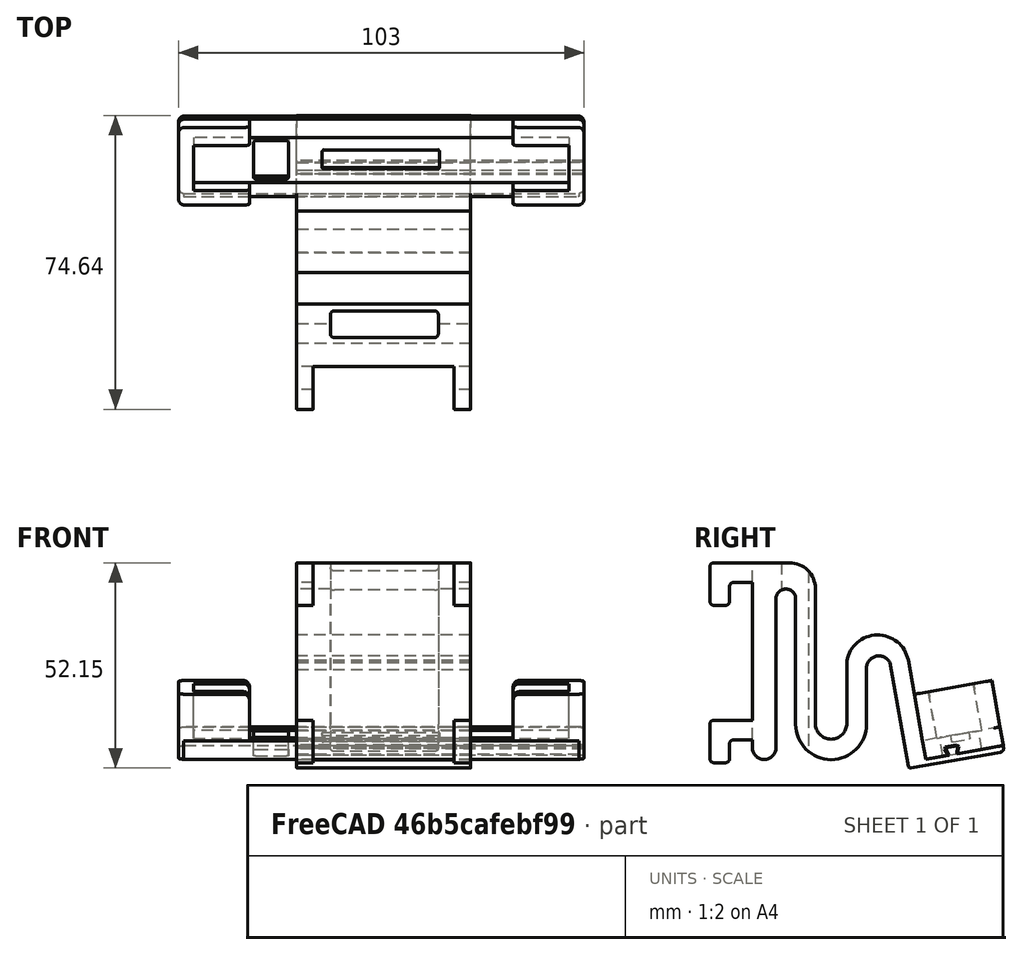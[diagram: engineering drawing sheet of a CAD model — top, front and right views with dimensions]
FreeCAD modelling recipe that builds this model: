
FCSTD DOCUMENT  (FreeCAD 1.1R20260414 (Git shallow))
Label: insight_skadis_holder_2
License: All rights reserved
LicenseURL: https://en.wikipedia.org/wiki/All_rights_reserved
objects: Sketcher::SketchObject×9, PartDesign::Fillet×7, PartDesign::Pocket×5, PartDesign::Pad×4, App::Point×2, PartDesign::Plane×2, PartDesign::Body×2, Part::Feature×1, Spreadsheet::Sheet×1, PartDesign::LinearPattern×1, Mesh::Feature×1
note: 73 computed .brp shape members not serialized (recipe doc carries the construction recipe); baked Part::Feature solids carry a one-line shape summary decoded from their .brp

FEATURE [App::Point] Origin001
  Role = Origin
FEATURE [Part::Feature] Path  label="Svg Import from Figma"
  Placement = pos=(0,0,0) rot=(0.57735,0.57735,0.57735;2.0944rad)
  shape: bbox 2e-07 x 45 x 37.5 mm, 1 faces, 0 solids (baked)
FEATURE [Spreadsheet::Sheet] Spreadsheet
  cells = A1='SkadisOffset; B1(SkadisOffset)=0.8; A2='SkadisHoleWidth; B2(SkadisHoleWidth)=5; A3='SkadisHoleHeight; B3(SkadisHoleHeight)=15; A4='SkadisHoleDistance; B4(SkadisHoleDistance)=35; A5='DeviceWidth; B5(DeviceWidth)=97; A6='DeviceDepth; B6(DeviceDepth)=14; A7='HolderWidth; B7(HolderWidth)==SkadisHoleDistance + HookThikness * 2 + SkadisOffset; A11='HookThikness; B11(HookThikness)==SkadisHoleWidth - SkadisOffset; C11='толщина в фас; A12='HookThiknessSide; B12(HookThiknessSide)==SkadisHoleHeight / 3; C12='толщина в профиль; A13='HookGrab; B13(HookGrab)==SkadisHoleWidth + SkadisOffset; C13='толщина захвата крюка; A14='UsbHoleWidth; B14(UsbHoleWidth)==HolderWidth - HookThikness * 4; A15='UsbHoleDepth; B15(UsbHoleDepth)=14; A16='UsbHoleOffset; B16(UsbHoleOffset)==HolderFirstWall + 1; A17='HolderFirstWall; B17(HolderFirstWall)=5.99; A18='HolderWallsThinkness; B18(HolderWallsThinkness)=5; A19='DeviceFrameFront; B19(DeviceFrameFront)=12; A20='DeviceIncline; B20(DeviceIncline)=100; A21='GrooveAngle; B21(GrooveAngle)=76; A22='GrooveWidthWide; B22(GrooveWidthWide)=3; A23='GroobeOffset; B23(GroobeOffset)=0.2; A24='FrameWall; B24(FrameWall)=3; A25='FilletRound; B25(FilletRound)=5; A26='GrooveChamber; B26(GrooveChamber)=0.5; C26='from back; A27='GrooveHolderHeight; B27(GrooveHolderHeight)=2; A28='GrooveHolderDepth; B28(GrooveHolderDepth)=1; A29='SensorHoleRightOffsetX; B29(SensorHoleRightOffsetX)=19; A30='SensorHoleRightOffsetY; B30(SensorHoleRightOffsetY)=2; A31='SensorHoleWidth; B31(SensorHoleWidth)=9; A32='SensorHoleHeight; B32(SensorHoleHeight)=10; A33='SensorHoleRadius; B33(SensorHoleRadius)=0.8; A34='ShelfFillet; B34(ShelfFillet)=1.5; A35='ShelfHolderFillet; B35(ShelfHolderFillet)=0.5; A36='HoldingEdgeTopOffset; B36(HoldingEdgeTopOffset)=6; A37='FrameHolderOffsetX; B37(FrameHolderOffsetX)=0.8; A38='FrameHolderOffsetY; B38(FrameHolderOffsetY)=1.2; A39='FrameHolderSDCardSlotWidth; B39(FrameHolderSDCardSlotWidth)=30; A40='FrameHolderSDCardSlotDepth; B40(FrameHolderSDCardSlotDepth)=5; A41='FrameHolderSDCardSlotDepthY; B41(FrameHolderSDCardSlotDepthY)=1.6; A42='FrameHolderSDCardSlotFillet; B42(FrameHolderSDCardSlotFillet)=0.35; A43='HooksDistance; B43(HooksDistance)==HolderWidth - HookThikness
FEATURE [Sketcher::SketchObject] Sketch
  ArcFitTolerance = 1e-06
  AttachmentSupport = -> [Origin]
  ExternalTypes = [0]
  FullyConstrained = false
  MakeInternals = false
  MapMode = 5
  Placement = pos=(0,0,0) rot=(0.57735,0.57735,0.57735;2.0944rad)
  _ExternalGeoVersion = 1
  expr: Constraints[18] = <<Spreadsheet>>.HolderFirstWall
  expr: Constraints[19] = <<Spreadsheet>>.HolderWallsThinkness
  expr: Constraints[20] = <<Spreadsheet>>.HolderWallsThinkness
  expr: Constraints[21] = <<Spreadsheet>>.HolderWallsThinkness
  expr: Constraints[24] = <<Spreadsheet>>.HolderWallsThinkness
  expr: Constraints[44] = <<Spreadsheet>>.DeviceIncline - 180
  expr: Constraints[48] = <<Spreadsheet>>.DeviceIncline - 180
  expr: Constraints[53] = <<Spreadsheet>>.GrooveAngle
  expr: Constraints[54] = <<Spreadsheet>>.GrooveAngle
  expr: Constraints[55] = <<Spreadsheet>>.DeviceDepth + <<Spreadsheet>>.FrameWall * 2
  expr: Constraints[56] = <<Spreadsheet>>.GrooveWidthWide
  sketch-geometry (33):
    g0: LineSegment StartX=-3e-16 StartY=0 StartZ=0 EndX=0 EndY=-46.9769 EndZ=0
    g1: ArcOfCircle CenterX=2.99501 CenterY=-46.9769 CenterZ=0 NormalX=0 NormalY=0 NormalZ=1 AngleXU=0 Radius=2.99501 StartAngle=3.14159 EndAngle=6.28319
    g2: LineSegment StartX=5.99001 StartY=-46.9769 StartZ=0 EndX=5.99 EndY=-9.16522 EndZ=0
    g3: ArcOfCircle CenterX=8.49 CenterY=-9.16522 CenterZ=0 NormalX=0 NormalY=0 NormalZ=1 AngleXU=0 Radius=2.5 StartAngle=2e-16 EndAngle=3.14159
    g4: LineSegment StartX=10.99 StartY=-9.16522 StartZ=0 EndX=10.99 EndY=-41.0251 EndZ=0
    g5: ArcOfCircle CenterX=19.99 CenterY=-41.0251 CenterZ=0 NormalX=0 NormalY=0 NormalZ=1 AngleXU=0 Radius=9 StartAngle=3.14159 EndAngle=6.28319
    g6: LineSegment StartX=28.99 StartY=-41.0251 StartZ=0 EndX=28.99 EndY=-27.153 EndZ=0
    g7: ArcOfCircle CenterX=19.99 CenterY=-40.8168 CenterZ=0 NormalX=0 NormalY=0 NormalZ=1 AngleXU=0 Radius=4 StartAngle=3.14159 EndAngle=6.28319
    g8: LineSegment StartX=15.99 StartY=-40.8168 StartZ=0 EndX=15.99 EndY=-6.59203 EndZ=0
    g9: ArcOfCircle CenterX=9.39799 CenterY=-6.59203 CenterZ=0 NormalX=0 NormalY=0 NormalZ=1 AngleXU=0 Radius=6.59202 StartAngle=6.28318 EndAngle=7.85398
    g10: LineSegment StartX=9.398 StartY=-6.32678e-06 StartZ=0 EndX=-3e-16 EndY=0 EndZ=0
    g11: LineSegment StartX=39.0323 StartY=-48.5109 StartZ=0 EndX=34.9541 EndY=-25.3824 EndZ=0
    g12: GeomPoint [constr] X=44.0323 Y=-49.9195 Z=0
    g13: LineSegment StartX=39.0323 StartY=-48.5109 StartZ=0 EndX=39.5932 EndY=-51.6921 EndZ=0
    g14: LineSegment StartX=40.2284 StartY=-52.1368 StartZ=0 EndX=63.0148 EndY=-48.119 EndZ=0
    g15: LineSegment StartX=63.7284 StartY=-46.4465 StartZ=0 EndX=57.8196 EndY=-47.4884 EndZ=0
    g16: ArcOfCircle CenterX=40.1332 CenterY=-51.5969 CenterZ=0 NormalX=0 NormalY=0 NormalZ=1 AngleXU=0 Radius=0.548294 StartAngle=3.31613 EndAngle=4.88692
    g17: GeomPoint [constr] X=39.6884 Y=-52.2321 Z=0
    g18: LineSegment StartX=63.7284 StartY=-46.4465 StartZ=0 EndX=63.8204 EndY=-46.9684 EndZ=0
    g19: ArcOfCircle CenterX=62.8424 CenterY=-47.1409 CenterZ=0 NormalX=0 NormalY=0 NormalZ=1 AngleXU=0 Radius=0.993179 StartAngle=4.88692 EndAngle=6.45772
    g20: LineSegment StartX=44.0323 StartY=-49.9195 StartZ=0 EndX=49.9411 EndY=-48.8776 EndZ=0
    g21: LineSegment StartX=49.9411 StartY=-48.8776 StartZ=0 EndX=49.1005 EndY=-46.9895 EndZ=0
    g22: LineSegment StartX=49.1005 StartY=-46.9895 StartZ=0 EndX=52.0549 EndY=-46.4685 EndZ=0
    g23: LineSegment StartX=52.0549 StartY=-46.4685 StartZ=0 EndX=51.9107 EndY=-48.5303 EndZ=0
    g24: LineSegment StartX=51.9107 StartY=-48.5303 StartZ=0 EndX=57.8196 EndY=-47.4884 EndZ=0
    g25: LineSegment [constr] StartX=47.7129 StartY=-49.2705 StartZ=0 EndX=47.9773 EndY=-50.7705 EndZ=0
    g26: LineSegment [constr] StartX=54.8651 StartY=-48.0093 StartZ=0 EndX=55.1296 EndY=-49.5093 EndZ=0
    g27: LineSegment [constr] StartX=49.9411 StartY=-48.8776 StartZ=0 EndX=51.9107 EndY=-48.5303 EndZ=0
    g28: ArcOfCircle CenterX=32.1407 CenterY=-26.8358 CenterZ=0 NormalX=0 NormalY=0 NormalZ=1 AngleXU=0 Radius=3.16663 StartAngle=0.476861 EndAngle=3.24193
    g29: LineSegment StartX=23.99 StartY=-24.9513 StartZ=0 EndX=23.99 EndY=-40.8168 EndZ=0
    g30: GeomPoint X=39.59 Y=-24.7261 Z=0
    g31: LineSegment StartX=39.59 StartY=-24.7261 StartZ=0 EndX=44.0323 EndY=-49.9195 EndZ=0
    g32: ArcOfCircle CenterX=31.8108 CenterY=-26.2828 CenterZ=0 NormalX=0 NormalY=0 NormalZ=1 AngleXU=0 Radius=7.93339 StartAngle=0.19751 EndAngle=2.97295
  constraints (66):
    c: Coincident(g-1,g0)
    c: PointOnObject(g0,g-2)
    c: Tangent(g0,g1) = -1.5708
    c: Angle(g1) = 3.14159
    c: Tangent(g1,g2) = -1.5708
    c: Tangent(g2,g3) = 1.5708
    c: Angle(g3) = 3.14159
    c: Tangent(g3,g4) = 1.5708
    c: Tangent(g4,g5) = -1.5708
    c: Angle(g5) = 3.14159
    c: Tangent(g5,g6) = -1.5708
    c: Coincident(g29,g7) = 1.5708
    c: Angle(g7) = 3.14159
    c: Tangent(g7,g8) = 1.5708
    c: Tangent(g8,g9) = -1.5708
    c: Angle(g9) = 1.5708
    c: Tangent(g9,g10) = -1.5708
    c: Coincident(g10,g0)
    c: DistanceX(g0,g2) = 5.99
    c: DistanceX(g29,g5) = 5
    c: DistanceX(g4,g7) = 5
    c: DistanceX(g2,g3) = 5
    c: DistanceX(g7,g29) = 8
    c: Coincident(g13,g11)
    c: DistanceX(g11,g12) = 5
    c: PointOnObject(g17,g13)
    c: PointOnObject(g17,g14)
    c: Tangent(g13,g16) = -1.5708
    c: Tangent(g14,g16) = -1.5708
    c: Tangent(g18,g19) = 1.5708
    c: Tangent(g14,g19) = -1.5708
    c: Parallel(g18,g13)
    c: Coincident(g18,g15)
    c: Parallel(g14,g15)
    c: Coincident(g12,g20)
    c: Coincident(g20,g21)
    c: Coincident(g21,g22)
    c: Coincident(g22,g23)
    c: Coincident(g23,g24)
    c: Equal(g24,g20)
    c: Parallel(g22,g20)
    c: Equal(g24,g15)
    c: PointOnObject(g25,g20)
    c: PointOnObject(g25,g14)
    c: Angle(g25) = -1.39626
    c: DistanceY(g25,g25) = 1.5
    c: Symmetric(g24,g24,g26)
    c: PointOnObject(g26,g14)
    c: Angle(g26) = -1.39626
    c: DistanceY(g26,g26) = 1.5
    c: Coincident(g27,g20)
    c: Coincident(g27,g23)
    c: Parallel(g22,g27)
    c: Angle(g21,g22) = 1.32645
    c: Angle(g22,g23) = 1.32645
    c: Distance(g12,g15) = 20
    c: Distance(g22) = 3
    c: Coincident(g15,g24)
    c: Distance(g20) = 6
    c: Parallel(g11,g13)
    c: Coincident(g28,g6)
    c: Coincident(g28,g11)
    c: Coincident(g31,g30)
    c: Coincident(g31,g12)
    c: Coincident(g32,g29)
    c: Coincident(g32,g30)
FEATURE [PartDesign::Pad] Pad  label="Holder (Pad)"
  Direction = (1,0,0)
  Length = 44.2
  Length2 = 10
  Profile = -> Sketch
  ReferenceAxis = -> Sketch [N_Axis]
  Refine = true
  SideType = 0
  Suppressed = false
  Type = 0
  Type2 = 0
  expr: Length = <<Spreadsheet>>.HolderWidth
FEATURE [Sketcher::SketchObject] Sketch003
  ArcFitTolerance = 1e-06
  ExternalTypes = [0]
  FullyConstrained = true
  MakeInternals = false
  Placement = pos=(44.2,0,0) rot=(0.58,0.58,0.58;2.0944rad)
  _ExternalGeoVersion = 1
  expr: .Placement.Base.x = <<Spreadsheet>>.HolderWidth
  expr: Constraints[10] = <<Spreadsheet>>.HookThiknessSide
  expr: Constraints[11] = <<Spreadsheet>>.HookThiknessSide + <<Spreadsheet>>.HookGrab
  expr: Constraints[13] = <<Spreadsheet>>.HookThiknessSide + <<Spreadsheet>>.HookGrab
  expr: Constraints[5] = <<Spreadsheet>>.HookGrab
  expr: Constraints[8] = <<Spreadsheet>>.HookGrab
  sketch-geometry (15):
    g0: LineSegment StartX=0 StartY=0 StartZ=0 EndX=-9.8 EndY=0 EndZ=0
    g1: LineSegment StartX=0 StartY=-5 StartZ=0 EndX=0 EndY=0 EndZ=0
    g2: GeomPoint X=-10.8 Y=0 Z=0
    g3: LineSegment StartX=0 StartY=-5 StartZ=0 EndX=-4.8 EndY=-5 EndZ=0
    g4: LineSegment StartX=-5.8 StartY=-6 StartZ=0 EndX=-5.8 EndY=-9.8 EndZ=0
    g5: LineSegment StartX=-10.8 StartY=-1 StartZ=0 EndX=-10.8 EndY=-9.8 EndZ=0
    g6: LineSegment StartX=-6.8 StartY=-10.8 StartZ=0 EndX=-9.8 EndY=-10.8 EndZ=0
    g7: ArcOfCircle CenterX=-9.8 CenterY=-1 CenterZ=0 NormalX=0 NormalY=0 NormalZ=1 AngleXU=0 Radius=1 StartAngle=1.5708 EndAngle=3.14159
    g8: GeomPoint [constr] X=-10.8 Y=0 Z=0
    g9: ArcOfCircle CenterX=-4.8 CenterY=-6 CenterZ=0 NormalX=0 NormalY=0 NormalZ=1 AngleXU=0 Radius=1 StartAngle=1.5708 EndAngle=3.14159
    g10: GeomPoint [constr] X=-5.8 Y=-5 Z=0
    g11: ArcOfCircle CenterX=-9.8 CenterY=-9.8 CenterZ=0 NormalX=0 NormalY=0 NormalZ=1 AngleXU=0 Radius=1 StartAngle=3.14159 EndAngle=4.71239
    g12: GeomPoint [constr] X=-10.8 Y=-10.8 Z=0
    g13: ArcOfCircle CenterX=-6.8 CenterY=-9.8 CenterZ=0 NormalX=0 NormalY=0 NormalZ=1 AngleXU=0 Radius=1 StartAngle=4.71239 EndAngle=6.28319
    g14: GeomPoint [constr] X=-5.8 Y=-10.8 Z=0
  constraints (34):
    c: Coincident(g-1,g0)
    c: Vertical(g1)
    c: Coincident(g1,g0)
    c: Coincident(g2,g8)
    c: Horizontal(g0)
    c: Distance(g3,g10) = 5.8
    c: Horizontal(g3)
    c: Coincident(g3,g1)
    c: Distance(g14,g10) = 5.8
    c: Vertical(g4)
    c: DistanceY(g1,g1) = 5
    c: Distance(g12,g8) = 10.8
    c: Vertical(g5)
    c: DistanceX(g8,g0) = 10.8
    c: PointOnObject(g8,g5)
    c: PointOnObject(g8,g0)
    c: Tangent(g5,g7) = -1.5708
    c: Tangent(g0,g7) = -1.5708
    c: Radius(g7) = 1
    c: PointOnObject(g10,g3)
    c: PointOnObject(g10,g4)
    c: Tangent(g3,g9) = -1.5708
    c: Tangent(g4,g9) = -1.5708
    c: Radius(g9) = 1
    c: PointOnObject(g12,g5)
    c: PointOnObject(g12,g6)
    c: Tangent(g5,g11) = -1.5708
    c: Tangent(g6,g11) = 1.5708
    c: Radius(g11) = 1
    c: PointOnObject(g14,g4)
    c: PointOnObject(g14,g6)
    c: Tangent(g4,g13) = 1.5708
    c: Tangent(g6,g13) = 1.5708
    c: Radius(g13) = 1
FEATURE [PartDesign::Pad] Pad001  label="Hook (Pad)"
  BaseFeature = -> Pad
  Direction = (1,-1e-16,2e-16)
  Length = 4.2
  Length2 = 10
  Profile = -> Sketch003
  ReferenceAxis = -> Sketch003 [N_Axis]
  Refine = true
  Reversed = true
  SideType = 0
  Suppressed = false
  Type = 0
  Type2 = 0
  expr: Length = <<Spreadsheet>>.HookThikness
FEATURE [PartDesign::LinearPattern] LinearPattern  label="Hooks (LinearPattern)"
  BaseFeature = -> Pad001
  Direction = -> X_Axis
  Direction2 = -> Z_Axis
  Length = 40
  Length2 = 40
  Mode = 0
  Mode2 = 1
  Occurrences = 2
  Occurrences2 = 2
  Offset = 40
  Offset2 = 40
  Originals = -> [Pad001]
  Refine = true
  Reversed = true
  Reversed2 = true
  SpacingPattern = [-45]
  SpacingPattern2 = [0]
  Spacings = [-1]
  Spacings2 = [-1]
  Suppressed = false
  TransformMode = 0
  expr: Length = <<Spreadsheet>>.HooksDistance
FEATURE [PartDesign::Plane] DatumPlane001
  AttachmentSupport = -> [LinearPattern]
  Length = 84.881
  MapMode = 5
  Placement = pos=(0,0,0) rot=(-1.00052,0,0;1e-06rad)
  ResizeMode = 0
  Width = 104.515
FEATURE [Sketcher::SketchObject] Sketch004
  ArcFitTolerance = 1e-06
  AttachmentSupport = -> [DatumPlane001]
  ExternalTypes = [0]
  FullyConstrained = false
  MakeInternals = false
  MapMode = 5
  Placement = pos=(0,0,0) rot=(-1.00052,0,0;1e-06rad)
  _ExternalGeoVersion = 1
  expr: Constraints[1] = <<Spreadsheet>>.UsbHoleWidth
  sketch-geometry (18):
    g0: LineSegment StartX=31.8418 StartY=14.2194 StartZ=0 EndX=10.0362 EndY=14.2194 EndZ=0
    g1: GeomPoint [constr] X=35.9994 Y=14.2194 Z=0
    g2: GeomPoint [constr] X=35.9994 Y=7.3916 Z=0
    g3: LineSegment StartX=9.59944 StartY=14.2194 StartZ=0 EndX=10.0362 EndY=14.2194 EndZ=0
    g4: LineSegment StartX=31.8418 StartY=14.2194 StartZ=0 EndX=34.9994 EndY=14.2194 EndZ=0
    g5: LineSegment StartX=8.59944 StartY=13.2194 StartZ=0 EndX=8.59944 EndY=8.3916 EndZ=0
    g6: LineSegment StartX=9.59944 StartY=7.3916 StartZ=0 EndX=34.9994 EndY=7.3916 EndZ=0
    g7: LineSegment StartX=35.9994 StartY=8.3916 StartZ=0 EndX=35.9994 EndY=13.2194 EndZ=0
    g8: LineSegment [constr] StartX=0 StartY=10.8055 StartZ=0 EndX=8.59944 EndY=10.8055 EndZ=0
    g9: LineSegment [constr] StartX=44.5989 StartY=10.8055 StartZ=0 EndX=35.9994 EndY=10.8055 EndZ=0
    g10: ArcOfCircle CenterX=9.59944 CenterY=8.3916 CenterZ=0 NormalX=0 NormalY=0 NormalZ=1 AngleXU=0 Radius=1 StartAngle=3.14159 EndAngle=4.71239
    g11: GeomPoint [constr] X=8.59944 Y=7.3916 Z=0
    g12: ArcOfCircle CenterX=34.9994 CenterY=8.3916 CenterZ=0 NormalX=0 NormalY=0 NormalZ=1 AngleXU=0 Radius=1 StartAngle=4.71239 EndAngle=6.28319
    g13: GeomPoint [constr] X=35.9994 Y=7.3916 Z=0
    g14: ArcOfCircle CenterX=9.59944 CenterY=13.2194 CenterZ=0 NormalX=0 NormalY=0 NormalZ=1 AngleXU=0 Radius=1 StartAngle=1.5708 EndAngle=3.14159
    g15: GeomPoint [constr] X=8.59944 Y=14.2194 Z=0
    g16: ArcOfCircle CenterX=34.9994 CenterY=13.2194 CenterZ=0 NormalX=0 NormalY=0 NormalZ=1 AngleXU=0 Radius=1 StartAngle=0 EndAngle=1.5708
    g17: GeomPoint [constr] X=35.9994 Y=14.2194 Z=0
  constraints (37):
    c: Horizontal(g0)
    c: Distance(g15,g1) = 27.4
    c: Coincident(g3,g0)
    c: Horizontal(g3)
    c: Coincident(g0,g4)
    c: Coincident(g17,g1)
    c: Horizontal(g4)
    c: Coincident(g13,g2)
    c: Horizontal(g6)
    c: Vertical(g7)
    c: Horizontal(g8)
    c: PointOnObject(g8,g-2)
    c: Symmetric(g15,g11,g8)
    c: Horizontal(g9)
    c: Symmetric(g13,g17,g9)
    c: Equal(g8,g9)
    c: Perpendicular(g6,g5)
    c: PointOnObject(g11,g5)
    c: PointOnObject(g11,g6)
    c: Tangent(g5,g10) = -1.5708
    c: Tangent(g6,g10) = -1.5708
    c: Radius(g10) = 1
    c: PointOnObject(g13,g7)
    c: PointOnObject(g13,g6)
    c: Tangent(g7,g12) = -1.5708
    c: Tangent(g6,g12) = -1.5708
    c: Radius(g12) = 1
    c: PointOnObject(g15,g3)
    c: PointOnObject(g15,g5)
    c: Tangent(g3,g14) = 1.5708
    c: Tangent(g5,g14) = -1.5708
    c: Radius(g14) = 1
    c: PointOnObject(g17,g7)
    c: PointOnObject(g17,g4)
    c: Tangent(g7,g16) = -1.5708
    c: Tangent(g4,g16) = 1.5708
    c: Radius(g16) = 1
FEATURE [PartDesign::Pocket] Pocket  label="USB Hole (Pocket)"
  BaseFeature = -> LinearPattern
  Direction = (0,-6.73205e-07,-1)
  Length = 5
  Length2 = 5
  Profile = -> Sketch004
  ReferenceAxis = -> Sketch004 [N_Axis]
  Refine = true
  SideType = 0
  Suppressed = false
  Type = 1
  Type2 = 0
FEATURE [PartDesign::Body] Body  label="Skadis Holder"
  AllowCompound = true
  Group = -> [Sketch,Pad,Sketch003,Pad001,LinearPattern,DatumPlane001,Sketch004,Pocket]
  Origin = -> Origin
  Tip = -> Pocket
FEATURE [App::Point] Origin003
  Role = Origin
FEATURE [Sketcher::SketchObject] Sketch005
  ArcFitTolerance = 1e-06
  AttachmentSupport = -> [Origin002]
  ExternalTypes = [0]
  FullyConstrained = false
  MakeInternals = false
  MapMode = 5
  Placement = pos=(0,0,0) rot=(0.57735,0.57735,0.57735;2.0944rad)
  _ExternalGeoVersion = 1
  expr: Constraints[2] = <<Spreadsheet>>.DeviceIncline
  expr: Constraints[6] = <<Spreadsheet>>.DeviceDepth + <<Spreadsheet>>.FrameWall * 2
  sketch-geometry (4):
    g0: LineSegment StartX=44.0319 StartY=-49.916 StartZ=0 EndX=43.2019 EndY=-45.2087 EndZ=0
    g1: LineSegment StartX=43.2019 StartY=-45.2087 StartZ=0 EndX=62.8981 EndY=-41.7357 EndZ=0
    g2: LineSegment StartX=62.8981 StartY=-41.7357 StartZ=0 EndX=63.7281 EndY=-46.4431 EndZ=0
    g3: LineSegment StartX=44.0319 StartY=-49.916 StartZ=0 EndX=63.7281 EndY=-46.4431 EndZ=0
  constraints (10):
    c: Coincident(g0,g1)
    c: Coincident(g1,g2)
    c: Angle(g0) = 1.74533
    c: Parallel(g2,g0)
    c: Perpendicular(g0,g1)
    c: Equal(g0,g2)
    c: Distance(g1) = 20
    c: Distance(g2) = 4.78
    c: Coincident(g3,g0)
    c: Coincident(g3,g2)
FEATURE [PartDesign::Pad] Pad002
  Direction = (1,0,0)
  Length = 103
  Length2 = 10
  Profile = -> Sketch005
  ReferenceAxis = -> Sketch005 [N_Axis]
  Refine = true
  SideType = 0
  Suppressed = false
  Type = 0
  Type2 = 0
  expr: Length = <<Spreadsheet>>.DeviceWidth + <<Spreadsheet>>.FrameWall * 2
FEATURE [Sketcher::SketchObject] Sketch009
  ArcFitTolerance = 1e-06
  AttachmentSupport = -> [Pad002]
  ExternalTypes = [0]
  FullyConstrained = false
  MakeInternals = false
  MapMode = 5
  Placement = pos=(0,9.03383,-51.2334) rot=(1,0,0;0.174533rad)
  _ExternalGeoVersion = 1
  expr: Constraints[11] = <<Spreadsheet>>.FrameWall + <<Spreadsheet>>.FrameHolderOffsetX
  expr: Constraints[22] = <<Spreadsheet>>.DeviceWidth - <<Spreadsheet>>.FrameHolderOffsetX * 2
  expr: Constraints[23] = <<Spreadsheet>>.DeviceDepth - <<Spreadsheet>>.FrameHolderOffsetY * 2
  expr: Constraints[24] = <<Spreadsheet>>.FrameWall + <<Spreadsheet>>.FrameHolderOffsetX
  expr: Constraints[8] = <<Spreadsheet>>.DeviceWidth + <<Spreadsheet>>.FrameWall * 2
  expr: Constraints[9] = <<Spreadsheet>>.DeviceDepth + <<Spreadsheet>>.FrameWall * 2
  sketch-geometry (10):
    g0: LineSegment StartX=0 StartY=54.6834 StartZ=0 EndX=0 EndY=34.6834 EndZ=0
    g1: LineSegment StartX=0 StartY=34.6834 StartZ=0 EndX=103 EndY=34.6834 EndZ=0
    g2: LineSegment StartX=103 StartY=34.6834 StartZ=0 EndX=103 EndY=54.6834 EndZ=0
    g3: LineSegment StartX=103 StartY=54.6834 StartZ=0 EndX=0 EndY=54.6834 EndZ=0
    g4: LineSegment [constr] StartX=0 StartY=44.6834 StartZ=0 EndX=3.8 EndY=44.6834 EndZ=0
    g5: LineSegment StartX=3.80763 StartY=50.0008 StartZ=0 EndX=3.80763 EndY=38.4008 EndZ=0
    g6: LineSegment StartX=3.80763 StartY=38.4008 StartZ=0 EndX=99.2076 EndY=38.4008 EndZ=0
    g7: LineSegment StartX=99.2076 StartY=38.4008 StartZ=0 EndX=99.2076 EndY=50.0008 EndZ=0
    g8: LineSegment StartX=99.2076 StartY=50.0008 StartZ=0 EndX=3.80763 EndY=50.0008 EndZ=0
    g9: LineSegment [constr] StartX=103 StartY=44.6834 StartZ=0 EndX=99.2 EndY=44.6834 EndZ=0
  constraints (27):
    c: Coincident(g0,g1)
    c: Coincident(g1,g2)
    c: Coincident(g2,g3)
    c: Coincident(g3,g0)
    c: Vertical(g0)
    c: Vertical(g2)
    c: Horizontal(g1)
    c: Horizontal(g3)
    c: Distance(g0,g2) = 103
    c: Distance(g1,g3) = 20
    c: PointOnObject(g0,g-2)
    c: Distance(g4) = 3.8
    c: Horizontal(g4)
    c: Symmetric(g0,g0,g4)
    c: Coincident(g5,g6)
    c: Coincident(g6,g7)
    c: Coincident(g7,g8)
    c: Coincident(g8,g5)
    c: Vertical(g5)
    c: Vertical(g7)
    c: Horizontal(g6)
    c: Horizontal(g8)
    c: Distance(g5,g7) = 95.4
    c: Distance(g6,g8) = 11.6
    c: Distance(g9) = 3.8
    c: Horizontal(g9)
    c: Symmetric(g2,g2,g9)
FEATURE [PartDesign::Pad] Pad003
  BaseFeature = -> Pad002
  Direction = (0,-0.173648,0.984808)
  Length = 12
  Length2 = 10
  Profile = -> Sketch009
  ReferenceAxis = -> Sketch009 [N_Axis]
  Refine = true
  SideType = 0
  Suppressed = false
  Type = 0
  Type2 = 0
  expr: Length = <<Spreadsheet>>.DeviceFrameFront
FEATURE [Sketcher::SketchObject] Sketch010
  ArcFitTolerance = 1e-06
  ExternalTypes = [0]
  FullyConstrained = false
  MakeInternals = false
  MapMode = 5
  Placement = pos=(0,37.8174,6.66822) rot=(0,0.642788,0.766044;3.14159rad)
  _ExternalGeoVersion = 1
  sketch-geometry (6):
    g0: LineSegment [constr] StartX=-100.11 StartY=-47.675 StartZ=0 EndX=-85.1099 EndY=-47.675 EndZ=0
    g1: LineSegment [constr] StartX=-3.08234 StartY=-47.5026 StartZ=0 EndX=-18.0823 EndY=-47.5026 EndZ=0
    g2: LineSegment StartX=-85.0318 StartY=-39.964 StartZ=0 EndX=-85.0318 EndY=-52.0176 EndZ=0
    g3: LineSegment StartX=-85.0318 StartY=-52.0176 StartZ=0 EndX=-18.0024 EndY=-52.0176 EndZ=0
    g4: LineSegment StartX=-18.0024 StartY=-52.0176 StartZ=0 EndX=-18.0024 EndY=-39.964 EndZ=0
    g5: LineSegment StartX=-18.0024 StartY=-39.964 StartZ=0 EndX=-85.0318 EndY=-39.964 EndZ=0
  constraints (12):
    c: Distance(g0) = 15
    c: Horizontal(g0)
    c: Distance(g1) = 15
    c: Horizontal(g1)
    c: Coincident(g2,g3)
    c: Coincident(g3,g4)
    c: Coincident(g4,g5)
    c: Coincident(g5,g2)
    c: Vertical(g2)
    c: Vertical(g4)
    c: Horizontal(g3)
    c: Horizontal(g5)
FEATURE [PartDesign::Pocket] Pocket004  label="CenterEmptySpace Pocket004"
  BaseFeature = -> Pad003
  Direction = (-1e-16,-0.984808,-0.173648)
  Length = 5
  Length2 = 5
  Profile = -> Sketch010
  ReferenceAxis = -> Sketch010 [N_Axis]
  Refine = true
  SideType = 2
  Suppressed = false
  Type = 1
  Type2 = 0
FEATURE [Sketcher::SketchObject] Sketch016
  ArcFitTolerance = 1e-06
  ExternalTypes = [0]
  FullyConstrained = false
  MakeInternals = false
  Placement = pos=(0,9.86387,-55.9408) rot=(1,0,0;3.31613rad)
  _ExternalGeoVersion = 1
  expr: Constraints[12] = <<Spreadsheet>>.SensorHoleRightOffsetY
  expr: Constraints[17] = <<Spreadsheet>>.SensorHoleRadius
  expr: Constraints[22] = <<Spreadsheet>>.SensorHoleRadius
  expr: Constraints[31] = <<Spreadsheet>>.SensorHoleRadius
  expr: Constraints[32] = <<Spreadsheet>>.SensorHoleRadius
  expr: Constraints[4] = <<Spreadsheet>>.SensorHoleWidth
  expr: Constraints[5] = <<Spreadsheet>>.SensorHoleHeight
  expr: Constraints[6] = <<Spreadsheet>>.SensorHoleRightOffsetX
  sketch-geometry (14):
    g0: LineSegment StartX=19 StartY=-39.9842 StartZ=0 EndX=19 EndY=-48.3842 EndZ=0
    g1: LineSegment StartX=19.8 StartY=-49.1842 StartZ=0 EndX=27.2 EndY=-49.1842 EndZ=0
    g2: LineSegment StartX=28 StartY=-48.3842 StartZ=0 EndX=28 EndY=-39.9842 EndZ=0
    g3: LineSegment StartX=27.2 StartY=-39.1842 StartZ=0 EndX=19.8 EndY=-39.1842 EndZ=0
    g4: LineSegment [constr] StartX=0 StartY=-44.1842 StartZ=0 EndX=19 EndY=-44.1842 EndZ=0
    g5: LineSegment [constr] StartX=19.9582 StartY=-37.1842 StartZ=0 EndX=19.9582 EndY=-39.1842 EndZ=0
    g6: ArcOfCircle CenterX=19.8 CenterY=-39.9842 CenterZ=0 NormalX=0 NormalY=0 NormalZ=1 AngleXU=0 Radius=0.8 StartAngle=1.5708 EndAngle=3.14159
    g7: GeomPoint [constr] X=19 Y=-39.1842 Z=0
    g8: ArcOfCircle CenterX=19.8 CenterY=-48.3842 CenterZ=0 NormalX=0 NormalY=0 NormalZ=1 AngleXU=0 Radius=0.8 StartAngle=3.14159 EndAngle=4.71239
    g9: GeomPoint [constr] X=19 Y=-49.1842 Z=0
    g10: ArcOfCircle CenterX=27.2 CenterY=-39.9842 CenterZ=0 NormalX=0 NormalY=0 NormalZ=1 AngleXU=0 Radius=0.8 StartAngle=3.3e-15 EndAngle=1.5708
    g11: GeomPoint [constr] X=28 Y=-39.1842 Z=0
    g12: ArcOfCircle CenterX=27.2 CenterY=-48.3842 CenterZ=0 NormalX=0 NormalY=0 NormalZ=1 AngleXU=0 Radius=0.8 StartAngle=4.71239 EndAngle=6.28319
    g13: GeomPoint [constr] X=28 Y=-49.1842 Z=0
  constraints (33):
    c: Vertical(g0)
    c: Vertical(g2)
    c: Horizontal(g1)
    c: Horizontal(g3)
    c: Distance(g7,g11) = 9
    c: Distance(g9,g7) = 10
    c: Distance(g4) = 19
    c: Horizontal(g4)
    c: PointOnObject(g4,g-2)
    c: Symmetric(g7,g9,g4)
    c: PointOnObject(g5,g3)
    c: Vertical(g5)
    c: DistanceY(g5,g5) = 2
    c: PointOnObject(g7,g0)
    c: PointOnObject(g7,g3)
    c: Tangent(g0,g6) = -1.5708
    c: Tangent(g3,g6) = -1.5708
    c: Radius(g6) = 0.8
    c: PointOnObject(g9,g0)
    c: PointOnObject(g9,g1)
    c: Tangent(g0,g8) = -1.5708
    c: Tangent(g1,g8) = -1.5708
    c: Radius(g8) = 0.8
    c: PointOnObject(g11,g2)
    c: PointOnObject(g11,g3)
    c: Tangent(g2,g10) = -1.5708
    c: Tangent(g3,g10) = -1.5708
    c: PointOnObject(g13,g1)
    c: PointOnObject(g13,g2)
    c: Tangent(g1,g12) = -1.5708
    c: Tangent(g2,g12) = -1.5708
    c: Radius(g10) = 0.8
    c: Radius(g12) = 0.8
FEATURE [PartDesign::Pocket] Pocket005  label="SensorHole"
  BaseFeature = -> Pocket004
  Direction = (0,-0.173648,0.984808)
  Length = 5
  Length2 = 5
  Profile = -> Sketch016
  ReferenceAxis = -> Sketch016 [N_Axis]
  Refine = true
  SideType = 0
  Suppressed = false
  Type = 1
  Type2 = 0
FEATURE [Mesh::Feature] Altruist_Insight_2_Device  label="Altruist_Insight_2-Device"
  Placement = pos=(23,47.6136,-3.99481) rot=(0,-0.087156,0.996195;3.14159rad)
FEATURE [Sketcher::SketchObject] Sketch017
  ArcFitTolerance = 1e-06
  AttachmentSupport = -> [Pocket005]
  ExternalTypes = [0]
  FullyConstrained = false
  MakeInternals = false
  MapMode = 5
  Placement = pos=(0,9.03383,-51.2334) rot=(1,0,0;0.174533rad)
  _ExternalGeoVersion = 1
  expr: Constraints[44] = <<Spreadsheet>>.FrameHolderSDCardSlotWidth / 2
  expr: Constraints[45] = <<Spreadsheet>>.FrameHolderSDCardSlotDepth / 2
  expr: Constraints[65] = <<Spreadsheet>>.FrameHolderSDCardSlotFillet
  expr: Constraints[8] = <<Spreadsheet>>.DeviceWidth - <<Spreadsheet>>.FrameHolderOffsetX * 2
  expr: Constraints[9] = <<Spreadsheet>>.DeviceDepth - <<Spreadsheet>>.FrameHolderOffsetY * 2
  sketch-geometry (27):
    g0: LineSegment [constr] StartX=3.79904 StartY=49.9317 StartZ=0 EndX=3.79904 EndY=38.3919 EndZ=0
    g1: LineSegment [constr] StartX=99.199 StartY=38.3816 StartZ=0 EndX=99.199 EndY=49.8627 EndZ=0
    g2: LineSegment [constr] StartX=3.79904 StartY=49.9816 StartZ=0 EndX=3.79904 EndY=38.3816 EndZ=0
    g3: LineSegment [constr] StartX=3.79904 StartY=38.3816 StartZ=0 EndX=51.499 EndY=38.3816 EndZ=0
    g4: LineSegment [constr] StartX=99.199 StartY=38.3816 StartZ=0 EndX=99.199 EndY=49.9816 EndZ=0
    g5: LineSegment [constr] StartX=99.199 StartY=49.9816 StartZ=0 EndX=51.499 EndY=49.9816 EndZ=0
    g6: LineSegment [constr] StartX=51.499 StartY=49.9816 StartZ=0 EndX=3.79904 EndY=49.9816 EndZ=0
    g7: LineSegment [constr] StartX=51.499 StartY=38.3816 StartZ=0 EndX=99.199 EndY=38.3816 EndZ=0
    g8: LineSegment [constr] StartX=51.499 StartY=49.9816 StartZ=0 EndX=51.499 EndY=44.1816 EndZ=0
    g9: LineSegment [constr] StartX=51.499 StartY=44.1816 StartZ=0 EndX=51.499 EndY=38.3816 EndZ=0
    g10: LineSegment [constr] StartX=51.499 StartY=44.1816 StartZ=0 EndX=31.9909 EndY=44.1816 EndZ=0
    g11: LineSegment [constr] StartX=51.499 StartY=44.1816 StartZ=0 EndX=68.2551 EndY=44.1816 EndZ=0
    g12: LineSegment StartX=36.499 StartY=44.1816 StartZ=0 EndX=36.499 EndY=46.3316 EndZ=0
    g13: LineSegment StartX=36.849 StartY=46.6816 StartZ=0 EndX=51.499 EndY=46.6816 EndZ=0
    g14: LineSegment StartX=51.499 StartY=46.6816 StartZ=0 EndX=65.9772 EndY=46.6816 EndZ=0
    g15: LineSegment StartX=66.3272 StartY=46.3316 StartZ=0 EndX=66.3272 EndY=42.2491 EndZ=0
    g16: LineSegment StartX=65.9772 StartY=41.8991 StartZ=0 EndX=51.499 EndY=41.8991 EndZ=0
    g17: LineSegment StartX=51.499 StartY=41.8991 StartZ=0 EndX=36.849 EndY=41.8991 EndZ=0
    g18: LineSegment StartX=36.499 StartY=42.2491 StartZ=0 EndX=36.499 EndY=44.1816 EndZ=0
    g19: ArcOfCircle CenterX=36.849 CenterY=46.3316 CenterZ=0 NormalX=0 NormalY=0 NormalZ=1 AngleXU=0 Radius=0.35 StartAngle=1.5708 EndAngle=3.14159
    g20: GeomPoint [constr] X=36.499 Y=46.6816 Z=0
    g21: ArcOfCircle CenterX=36.849 CenterY=42.2491 CenterZ=0 NormalX=0 NormalY=0 NormalZ=1 AngleXU=0 Radius=0.35 StartAngle=3.14159 EndAngle=4.71239
    g22: GeomPoint [constr] X=36.499 Y=41.8991 Z=0
    g23: ArcOfCircle CenterX=65.9772 CenterY=46.3316 CenterZ=0 NormalX=0 NormalY=0 NormalZ=1 AngleXU=0 Radius=0.35 StartAngle=8.4e-15 EndAngle=1.5708
    g24: GeomPoint [constr] X=66.3272 Y=46.6816 Z=0
    g25: ArcOfCircle CenterX=65.9772 CenterY=42.2491 CenterZ=0 NormalX=0 NormalY=0 NormalZ=1 AngleXU=0 Radius=0.35 StartAngle=4.71239 EndAngle=6.28319
    g26: GeomPoint [constr] X=66.3272 Y=41.8991 Z=0
  constraints (66):
    c: Vertical(g0)
    c: Vertical(g1)
    c: Coincident(g2,g3)
    c: Coincident(g7,g4)
    c: Coincident(g4,g5)
    c: Coincident(g6,g2)
    c: Vertical(g2)
    c: Vertical(g4)
    c: Distance(g2,g4) = 95.4
    c: Distance(g3,g6) = 11.6
    c: PointOnObject(g2,g0)
    c: Coincident(g7,g1)
    c: Horizontal(g5)
    c: Horizontal(g6)
    c: Coincident(g5,g6)
    c: Horizontal(g3)
    c: Horizontal(g7)
    c: Coincident(g3,g7)
    c: Equal(g6,g5)
    c: Equal(g3,g7)
    c: Coincident(g8,g5)
    c: Coincident(g9,g3)
    c: Coincident(g8,g9)
    c: Equal(g8,g9)
    c: Distance(g10) = 19.5081
    c: Horizontal(g10)
    c: Coincident(g10,g8)
    c: Distance(g11) = 16.756
    c: Horizontal(g11)
    c: Coincident(g11,g8)
    c: PointOnObject(g12,g10)
    c: Vertical(g12)
    c: PointOnObject(g13,g8)
    c: Horizontal(g13)
    c: Coincident(g13,g14)
    c: Horizontal(g14)
    c: Vertical(g15)
    c: PointOnObject(g16,g9)
    c: Horizontal(g16)
    c: Coincident(g16,g17)
    c: Horizontal(g17)
    c: Coincident(g18,g12)
    c: Vertical(g18)
    c: Parallel(g8,g9)
    c: DistanceX(g20,g13) = 15
    c: DistanceY(g12,g20) = 2.5
    c: PointOnObject(g20,g12)
    c: PointOnObject(g20,g13)
    c: Tangent(g12,g19) = 1.5708
    c: Tangent(g13,g19) = 1.5708
    c: PointOnObject(g22,g17)
    c: PointOnObject(g22,g18)
    c: Tangent(g17,g21) = 1.5708
    c: Tangent(g18,g21) = 1.5708
    c: PointOnObject(g24,g14)
    c: PointOnObject(g24,g15)
    c: Tangent(g14,g23) = 1.5708
    c: Tangent(g15,g23) = 1.5708
    c: PointOnObject(g26,g15)
    c: PointOnObject(g26,g16)
    c: Tangent(g15,g25) = 1.5708
    c: Tangent(g16,g25) = 1.5708
    c: Equal(g19,g21)
    c: Equal(g21,g23)
    c: Equal(g23,g25)
    c: Radius(g19) = 0.35
FEATURE [PartDesign::Pocket] Pocket006
  BaseFeature = -> Pocket005
  Direction = (0,0.173648,-0.984808)
  Length = 1.6
  Length2 = 5
  Profile = -> Sketch017
  ReferenceAxis = -> Sketch017 [N_Axis]
  Refine = true
  SideType = 0
  Suppressed = false
  Type = 0
  Type2 = 0
  expr: Length = <<Spreadsheet>>.FrameHolderSDCardSlotDepthY
FEATURE [PartDesign::Fillet] Fillet
  Base = -> Pocket006 [Edge19]
  BaseFeature = -> Pocket006
  Radius = 1.5
  Refine = true
  SupportTransform = false
  Suppressed = false
  UseAllEdges = false
  expr: Radius = <<Spreadsheet>>.ShelfFillet
FEATURE [PartDesign::Fillet] Fillet001
  Base = -> Fillet [Edge29]
  BaseFeature = -> Fillet
  Radius = 1.5
  Refine = true
  SupportTransform = false
  Suppressed = false
  UseAllEdges = false
  expr: Radius = <<Spreadsheet>>.ShelfFillet
FEATURE [PartDesign::Fillet] Fillet002
  Base = -> Fillet001 [Edge7]
  BaseFeature = -> Fillet001
  Radius = 1.5
  Refine = true
  SupportTransform = false
  Suppressed = false
  UseAllEdges = false
  expr: Radius = <<Spreadsheet>>.ShelfFillet
FEATURE [PartDesign::Fillet] Fillet003
  Base = -> Fillet002 [Edge40]
  BaseFeature = -> Fillet002
  Radius = 1.5
  Refine = true
  SupportTransform = false
  Suppressed = false
  UseAllEdges = false
  expr: Radius = <<Spreadsheet>>.ShelfFillet
FEATURE [PartDesign::Fillet] Fillet004
  Base = -> Fillet003 [Edge24]
  BaseFeature = -> Fillet003
  Radius = 1.5
  Refine = true
  SupportTransform = false
  Suppressed = false
  UseAllEdges = false
  expr: Radius = <<Spreadsheet>>.ShelfFillet
FEATURE [PartDesign::Fillet] Fillet005
  Base = -> Fillet004 [Edge14]
  BaseFeature = -> Fillet004
  Radius = 1.5
  Refine = true
  SupportTransform = false
  Suppressed = false
  UseAllEdges = false
  expr: Radius = <<Spreadsheet>>.ShelfFillet
FEATURE [PartDesign::Fillet] Fillet006
  Base = -> Fillet005 [Edge32,Edge31,Edge98,Edge97]
  BaseFeature = -> Fillet005
  Radius = 1.5
  Refine = true
  SupportTransform = false
  Suppressed = false
  UseAllEdges = false
  expr: Radius = <<Spreadsheet>>.ShelfFillet
FEATURE [PartDesign::Plane] DatumPlane
  AttachmentSupport = -> [Fillet006]
  Length = 105.034
  MapMode = 5
  Placement = pos=(103,0,0) rot=(0.57735,0.57735,0.57735;2.0944rad)
  ResizeMode = 0
  Width = 91.2221
FEATURE [Sketcher::SketchObject] Sketch018
  ArcFitTolerance = 1e-06
  AttachmentSupport = -> [DatumPlane]
  ExternalTypes = [0]
  FullyConstrained = false
  MakeInternals = false
  MapMode = 5
  Placement = pos=(103,0,0) rot=(0.57735,0.57735,0.57735;2.0944rad)
  _ExternalGeoVersion = 1
  expr: Constraints[17] = <<Spreadsheet>>.GroobeOffset
  expr: Constraints[2] = <<Spreadsheet>>.DeviceIncline
  sketch-geometry (16):
    g0: LineSegment StartX=49.8398 StartY=-48.8929 StartZ=0 EndX=48.8463 EndY=-47.3204 EndZ=0
    g1: LineSegment StartX=49.0814 StartY=-46.7888 StartZ=0 EndX=52.0133 EndY=-46.2718 EndZ=0
    g2: LineSegment StartX=52.4159 StartY=-46.692 StartZ=0 EndX=52.0144 EndY=-48.5094 EndZ=0
    g3: LineSegment StartX=52.0144 StartY=-48.5094 StartZ=0 EndX=49.8398 EndY=-48.8929 EndZ=0
    g4: LineSegment [constr] StartX=49.4775 StartY=-53.5977 StartZ=0 EndX=47.1626 EndY=-40.4691 EndZ=0
    g5: LineSegment [constr] StartX=49.1036 StartY=-46.9946 StartZ=0 EndX=48.6869 EndY=-47.0681 EndZ=0
    g6: LineSegment [constr] StartX=52.0612 StartY=-46.4845 StartZ=0 EndX=52.4779 EndY=-46.411 EndZ=0
    g7: LineSegment [constr] StartX=49.8212 StartY=-48.8634 StartZ=0 EndX=49.9295 EndY=-48.8443 EndZ=0
    g8: LineSegment [constr] StartX=52.0166 StartY=-48.4998 StartZ=0 EndX=51.9082 EndY=-48.5189 EndZ=0
    g9: LineSegment [constr] StartX=50.5482 StartY=-46.5301 StartZ=0 EndX=50.5829 EndY=-46.7271 EndZ=0
    g10: ArcOfCircle [constr] CenterX=49.1422 CenterY=-47.1335 CenterZ=0 NormalX=0 NormalY=0 NormalZ=1 AngleXU=0 Radius=0.35 StartAngle=1.74533 EndAngle=3.70507
    g11: GeomPoint [constr] X=48.5676 Y=-46.8794 Z=0
    g12: LineSegment StartX=49.0814 StartY=-46.7888 StartZ=0 EndX=48.8463 EndY=-47.3204 EndZ=0
    g13: ArcOfCircle [constr] CenterX=52.0741 CenterY=-46.6165 CenterZ=0 NormalX=0 NormalY=0 NormalZ=1 AngleXU=0 Radius=0.35 StartAngle=6.06579 EndAngle=8.02851
    g14: GeomPoint [constr] X=52.5288 Y=-46.1809 Z=0
    g15: LineSegment StartX=52.4159 StartY=-46.692 StartZ=0 EndX=52.0133 EndY=-46.2718 EndZ=0
  constraints (33):
    c: Coincident(g2,g3)
    c: Coincident(g3,g0)
    c: Angle(g4) = 1.74533
    c: Perpendicular(g4,g3)
    c: Parallel(g1,g3)
    c: PointOnObject(g5,g0)
    c: PointOnObject(g6,g2)
    c: Perpendicular(g4,g5)
    c: Perpendicular(g4,g6)
    c: Equal(g6,g5)
    c: PointOnObject(g7,g0)
    c: Perpendicular(g4,g7)
    c: PointOnObject(g8,g2)
    c: Perpendicular(g4,g8)
    c: Equal(g8,g7)
    c: Symmetric(g11,g14,g9)
    c: Parallel(g9,g4)
    c: Distance(g9) = 0.2
    c: Distance(g7) = 0.11
    c: PointOnObject(g11,g0)
    c: PointOnObject(g11,g1)
    c: Tangent(g0,g10) = 1.5708
    c: Tangent(g1,g10) = 1.5708
    c: Coincident(g12,g0)
    c: Coincident(g12,g1)
    c: PointOnObject(g14,g1)
    c: PointOnObject(g14,g2)
    c: Tangent(g1,g13) = 1.5708
    c: Tangent(g2,g13) = 1.5708
    c: Coincident(g15,g1)
    c: Coincident(g15,g2)
    c: Equal(g10,g13)
    c: Radius(g10) = 0.35
FEATURE [PartDesign::Pocket] Pocket007
  BaseFeature = -> Fillet006
  Direction = (-1,0,0)
  Length = 73
  Length2 = 5
  Profile = -> Sketch018
  ReferenceAxis = -> Sketch018 [N_Axis]
  Refine = true
  SideType = 0
  Suppressed = false
  Type = 0
  Type2 = 0
FEATURE [PartDesign::Body] Body001  label="Insight E-ink 4.2 shelf"
  AllowCompound = true
  Group = -> [Sketch005,Pad002,Sketch009,Pad003,Sketch010,Pocket004,Sketch016,Pocket005,Sketch017,Pocket006,Fillet,Fillet001,Fillet002,Fillet003,Fillet004,Fillet005,Fillet006,DatumPlane,Sketch018,Pocket007]
  Origin = -> Origin002
  Placement = pos=(-30,0,0) rot=(0,0,1;0rad)
  Tip = -> Pocket007
